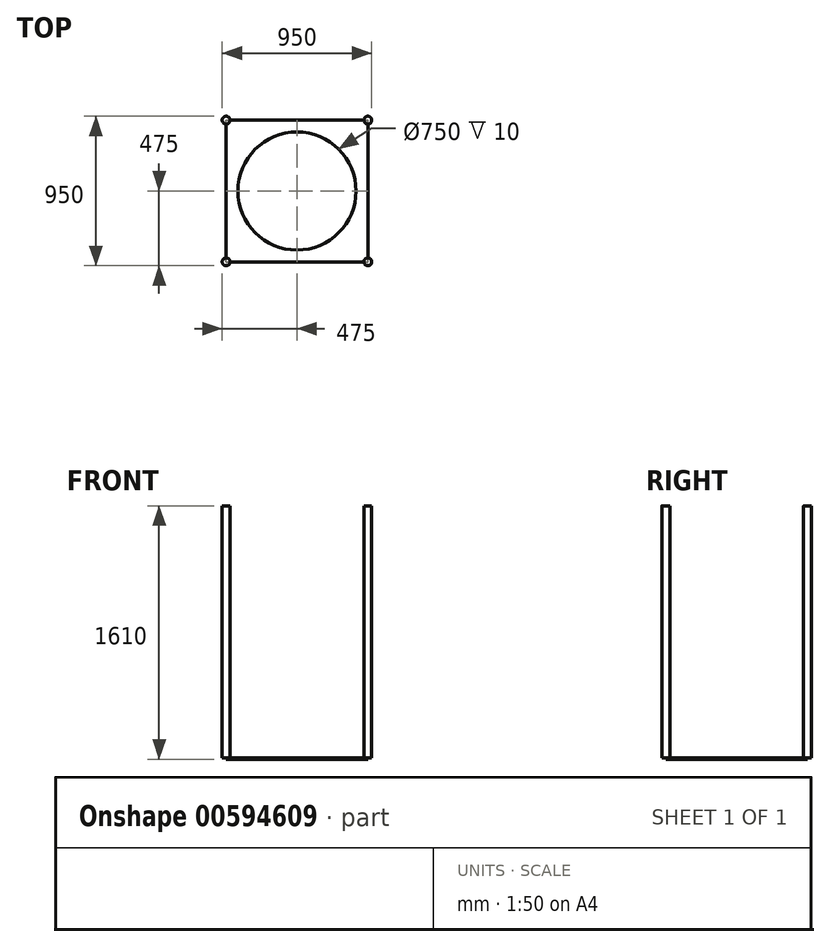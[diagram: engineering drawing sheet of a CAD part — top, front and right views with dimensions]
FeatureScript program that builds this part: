
annotation { "Feature Type Name" : "Feature", "Feature Type Description" : "" }
export const myFeature = defineFeature(function(context is Context, id is Id, definition is map)
    precondition{}
    {
        {
            var Q0;
            Q0=qCreatedBy(makeId("Top.planeOp"),FACE);
            var sketch = newSketch(context, id + "F0", { "sketchPlane" : qUnion([Q0])});
            skLineSegment(sketch, "E0.bottom", {"start": v(0, 0) * mm, "end": v(900, 0) * mm});
            skLineSegment(sketch, "E0.top", {"start": v(0, 900) * mm, "end": v(900, 900) * mm});
            skLineSegment(sketch, "E0.left", {"start": v(0, 0) * mm, "end": v(0, 900) * mm});
            skLineSegment(sketch, "E0.right", {"start": v(900, 0) * mm, "end": v(900, 900) * mm});
            skSolve(sketch);
        }
        {
            var Q0;
            Q0 = qSketchRegion(id + "F0", true);
            extrude(context, id + "F1", {"entities" : qUnion([Q0]), "depth" : 10 * mm, "offsetDistance" : 25 * mm});
        }
        {
            var Q0;
            Q0=makeQuery(id+"F1.opExtrude","CAP_FACE",FACE,{"disambiguationData":[OSD([sQuery(id+"F0.wireOp",EDGE,"E0.bottom"),sQuery(id+"F0.wireOp",EDGE,"E0.top"),sQuery(id+"F0.wireOp",EDGE,"E0.left"),sQuery(id+"F0.wireOp",EDGE,"E0.right")])],"isStart":false});
            var sketch = newSketch(context, id + "F2", { "sketchPlane" : qUnion([Q0])});
            skCircle(sketch, "E1", {"center": v(0, 0) * mm, "radius": 25 * mm});
            skCircle(sketch, "E2", {"center": v(0, 900) * mm, "radius": 25 * mm});
            skCircle(sketch, "E3", {"center": v(900, 900) * mm, "radius": 25 * mm});
            skCircle(sketch, "E4", {"center": v(900, 0) * mm, "radius": 25 * mm});
            skSolve(sketch);
        }
        {
            var Q0;
            Q0 = qSketchRegion(id + "F2", true);
            extrude(context, id + "F3", {"entities" : qUnion([Q0]), "operationType" : NewBodyOperationType.ADD, "depth" : 1600 * mm, "offsetDistance" : 25 * mm});
        }
        {
            var Q0;
            Q0=makeQuery(id+"F1.opExtrude","CAP_FACE",FACE,{"disambiguationData":[OSD([sQuery(id+"F0.wireOp",EDGE,"E0.bottom"),sQuery(id+"F0.wireOp",EDGE,"E0.top"),sQuery(id+"F0.wireOp",EDGE,"E0.left"),sQuery(id+"F0.wireOp",EDGE,"E0.right")])],"isStart":false});
            var sketch = newSketch(context, id + "F4", { "sketchPlane" : qUnion([Q0])});
            skCircle(sketch, "E5", {"center": v(450, 450) * mm, "radius": 375 * mm});
            skSolve(sketch);
        }
        {
            var Q0;
            Q0 = qSketchRegion(id + "F4", true);
            extrude(context, id + "F5", {"entities" : qUnion([Q0]), "operationType" : NewBodyOperationType.REMOVE, "endBound" : BoundingType.THROUGH_ALL, "oppositeDirection" : true, "depth" : 25 * mm, "offsetDistance" : 25 * mm});
        }
    });
